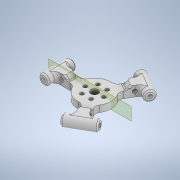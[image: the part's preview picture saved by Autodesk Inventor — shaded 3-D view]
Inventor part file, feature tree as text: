
AUTODESK INVENTOR PART (.ipt)
format: ipt  version: 2020 (Build 240168000, 168)  size: 663,552 bytes
history: native  units: mm
features: extrude x11, sketch x11, projected_geometry x7, pattern_circular x3, fillet x3, chamfer x3, thicken_offset x2, plane x1
ambient origin geometry x8: Origin, YZ Plane, XZ Plane, XY Plane, X Axis, Y Axis, Z Axis, Center Point
bodies: Solid1 (feature_tree)
feature tree (41):
  extrude  "Extrusion1"  Depth=30.0mm
  extrude  "Extrusion2"  Depth=10.0mm
  extrude  "Extrusion3"  Depth=5.0mm TaperAngle=0.0deg
  extrude  "Extrusion4"  Depth=5.0mm TaperAngle=0.0deg
  extrude  "Extrusion5"  Depth=5.0mm TaperAngle=0.0deg
  extrude  "Extrusion6"  Depth=4.0mm TaperAngle=0.0deg
  thicken_offset  "Thicken1"
  thicken_offset  "Thicken2"
  pattern_circular  "Circular Pattern1"  Count=2  [1 undecoded]
  extrude  "Extrusion7"  Depth=1.5mm
  fillet  "Fillet1"  Radius=1.5mm
  extrude  "Extrusion8"  Depth=30.0mm TaperAngle=360.0deg
  chamfer  "Chamfer1"  Distance=20.0mm
  fillet  "Fillet2"  Radius=6.0mm
  fillet  "Fillet3"  Radius=55.0mm
  extrude  "Extrusion9"  Depth=4.0mm TaperAngle=0.0deg
  pattern_circular  "Circular Pattern2"  Angle=45.0deg  [1 undecoded]
  extrude  "Extrusion10"  Depth=2.0mm
  plane  "Work Plane1"
  extrude  "Extrusion11"  Depth=4.0mm
  pattern_circular  "Circular Pattern3"  [2 undecoded]
  chamfer  "Chamfer2"  Distance=4.0mm
  chamfer  "Chamfer3"  Distance=10.0mm
  sketch  "Sketch1"  dims[d0=40.0mm d1=30.0mm]
  sketch  "Sketch2"  dims[d2=5.0mm d3=10.0mm]
  sketch  "Sketch3"  dims[d4=40.0mm d5=5.0mm d6=0.0mm]
  projected_geometry  "Projected Loop1"
  sketch  "Sketch4"  dims[d7=3.0mm d8=5.0mm d9=0.0mm]
  projected_geometry  "Projected Loop2"
  sketch  "Sketch5"  dims[d10=8.0mm d11=5.0mm d12=0.0mm]
  sketch  "Sketch6"  dims[d13=4.0mm d14=5.0mm d15=0.0mm]
  projected_geometry  "Projected Loop3"
  sketch  "Sketch7"  dims[d16=5.0mm d17=0.0mm]
  projected_geometry  "Projected Loop4"
  sketch  "Sketch8"  dims[d18=2.5mm d19=20.0mm d20=0.0mm]
  projected_geometry  "Projected Loop5"
  sketch  "Sketch9"  dims[d21=1.5mm d22=1.5mm d23=1.5mm]
  projected_geometry  "Projected Loop6"
  sketch  "Sketch10"  dims[d24=1.5mm d25=30.0mm d26=360.0deg]
  projected_geometry  "Projected Loop7"
  sketch  "Sketch11"  dims[d28=36.0mm d29=20.0mm d30=0.0mm d31=6.0mm d32=55.0mm d33=4.0mm d34=0.0mm d35=4.0mm d36=2.0mm d37=45.0deg d38=2.0mm d39=4.0mm d40=10.0mm d41=4.0mm d42=10.0mm d43=0.0mm d44=60.0mm d45=360.0deg d47=8.0mm d48=10.0mm d49=0.0mm d50=9.5mm d51=4.0mm d52=20.0mm d53=0.0mm d54=30.0mm d55=360.0deg d57=1.5mm d58=2.0mm d59=45.0deg d60=1.5mm d61=2.0mm d62=45.0deg]
note: 4 required parameter values undecoded (feature->parameter linkage not recoverable at this tier; creation-order binding heuristic only, values carry confidence <= 0.55)
